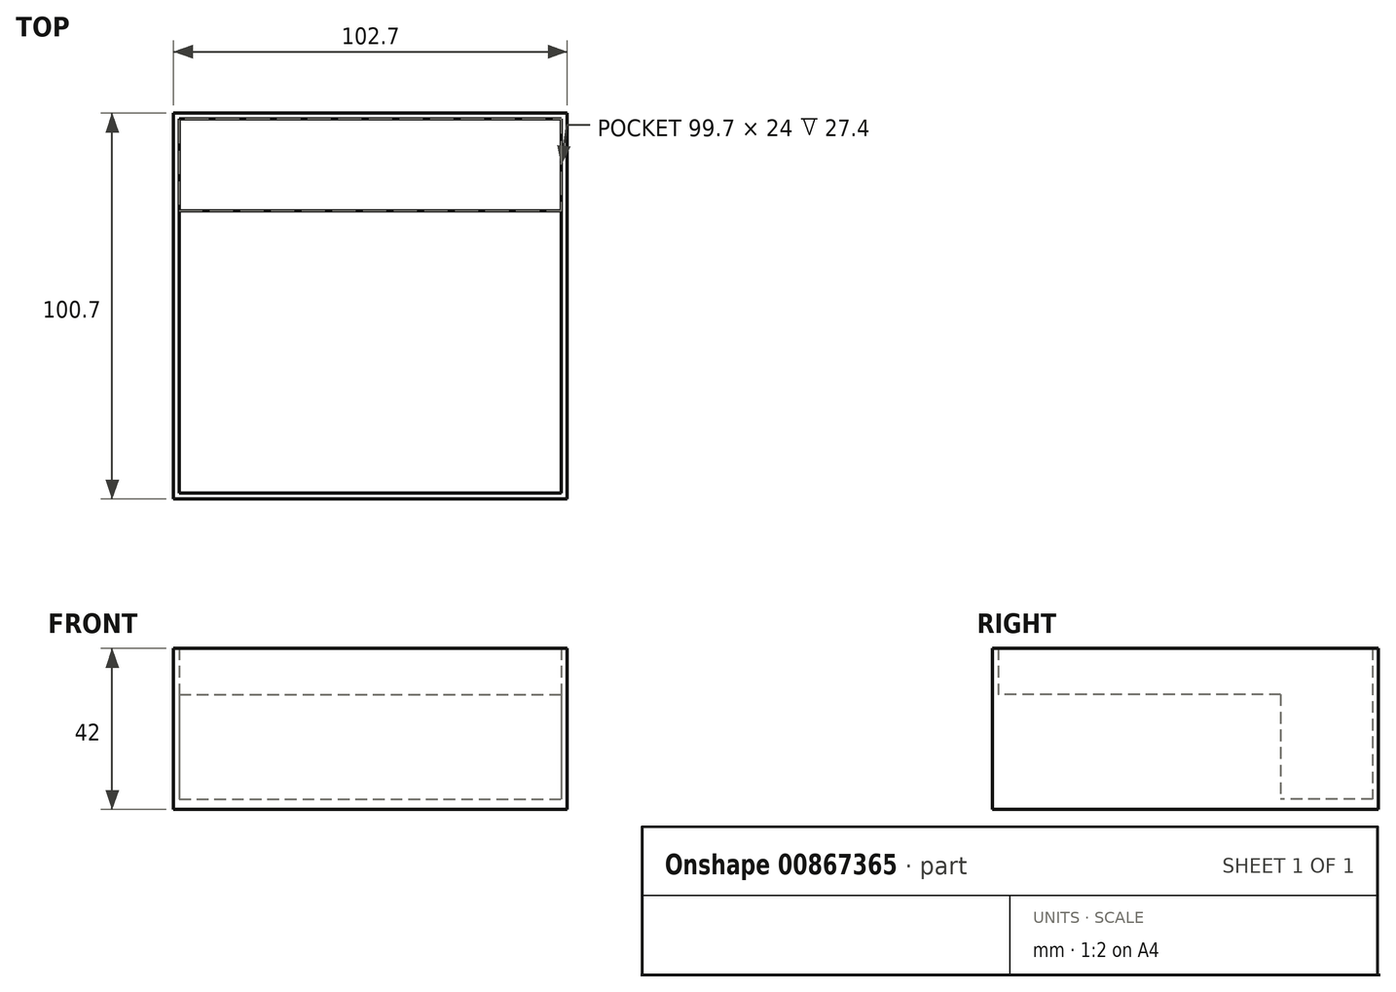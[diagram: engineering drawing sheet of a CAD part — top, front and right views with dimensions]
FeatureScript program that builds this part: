
annotation { "Feature Type Name" : "Feature", "Feature Type Description" : "" }
export const myFeature = defineFeature(function(context is Context, id is Id, definition is map)
    precondition{}
    {
        {
            var Q0;
            Q0=qCreatedBy(makeId("Top.planeOp"),FACE);
            var sketch = newSketch(context, id + "F0", { "sketchPlane" : qUnion([Q0])});
            skLineSegment(sketch, "E0.bottom", {"start": v(-49.85, 48.85) * mm, "end": v(49.85, 48.85) * mm});
            skLineSegment(sketch, "E0.top", {"start": v(-49.85, -48.85) * mm, "end": v(49.85, -48.85) * mm});
            skLineSegment(sketch, "E0.left", {"start": v(-49.85, 48.85) * mm, "end": v(-49.85, -48.85) * mm});
            skLineSegment(sketch, "E0.right", {"start": v(49.85, 48.85) * mm, "end": v(49.85, -48.85) * mm});
            skLineSegment(sketch, "E1", {"start": v(0, 63.1) * mm, "end": v(0, -64.8) * mm, "construction": true});
            skPoint(sketch, "E1.startSnap0", {"position": v(0, 48.85) * mm});
            skLineSegment(sketch, "E2", {"start": v(-65.65, 0) * mm, "end": v(53.75, 0) * mm, "construction": true});
            skPoint(sketch, "E2.startSnap0", {"position": v(-49.85, 0) * mm});
            skPoint(sketch, "E3", {"position": v(0, 0) * mm});
            skLineSegment(sketch, "E4.0", {"start": v(-51.35, 50.35) * mm, "end": v(51.35, 50.35) * mm});
            skLineSegment(sketch, "E4.1", {"start": v(-51.35, 50.35) * mm, "end": v(-51.35, -50.35) * mm});
            skLineSegment(sketch, "E4.2", {"start": v(-51.35, -50.35) * mm, "end": v(51.35, -50.35) * mm});
            skLineSegment(sketch, "E4.3", {"start": v(51.35, 50.35) * mm, "end": v(51.35, -50.35) * mm});
            skLineSegment(sketch, "E5", {"start": v(-49.85, 24.85) * mm, "end": v(49.85, 24.85) * mm});
            skSolve(sketch);
        }
        {
            var Q0;
            {var subQ0=sQuery(id+"F0.wireOp",EDGE,"E0.bottom");Q0=makeQuery(id+"F0.imprint","IMPRINT",FACE,{"disambiguationData":[TD([[makeQuery(id+"F0.imprint","IMPRINT",EDGE,{"derivedFrom":subQ0}),-1.0]])]});}
            extrude(context, id + "F1", {"entities" : qUnion([Q0]), "depth" : 2.6 * mm, "offsetDistance" : 25 * mm});
        }
        {
            var Q0;
            {var subQ0=sQuery(id+"F0.wireOp",EDGE,"E0.top");Q0=makeQuery(id+"F0.imprint","IMPRINT",FACE,{"disambiguationData":[TD([[makeQuery(id+"F0.imprint","IMPRINT",EDGE,{"derivedFrom":subQ0}),1.0]])]});}
            extrude(context, id + "F2", {"entities" : qUnion([Q0]), "operationType" : NewBodyOperationType.ADD, "depth" : 30 * mm, "offsetDistance" : 25 * mm});
        }
        {
            var Q0;
            {var subQ4=sQuery(id+"F0.wireOp",EDGE,"E0.bottom");Q0=makeQuery(id+"F0.imprint","IMPRINT",FACE,{"disambiguationData":[TD([[makeQuery(id+"F0.imprint","IMPRINT",EDGE,{"derivedFrom":subQ4}),1.0]])]});}
            extrude(context, id + "F3", {"entities" : qUnion([Q0]), "operationType" : NewBodyOperationType.ADD, "depth" : 42 * mm, "offsetDistance" : 25 * mm});
        }
    });
